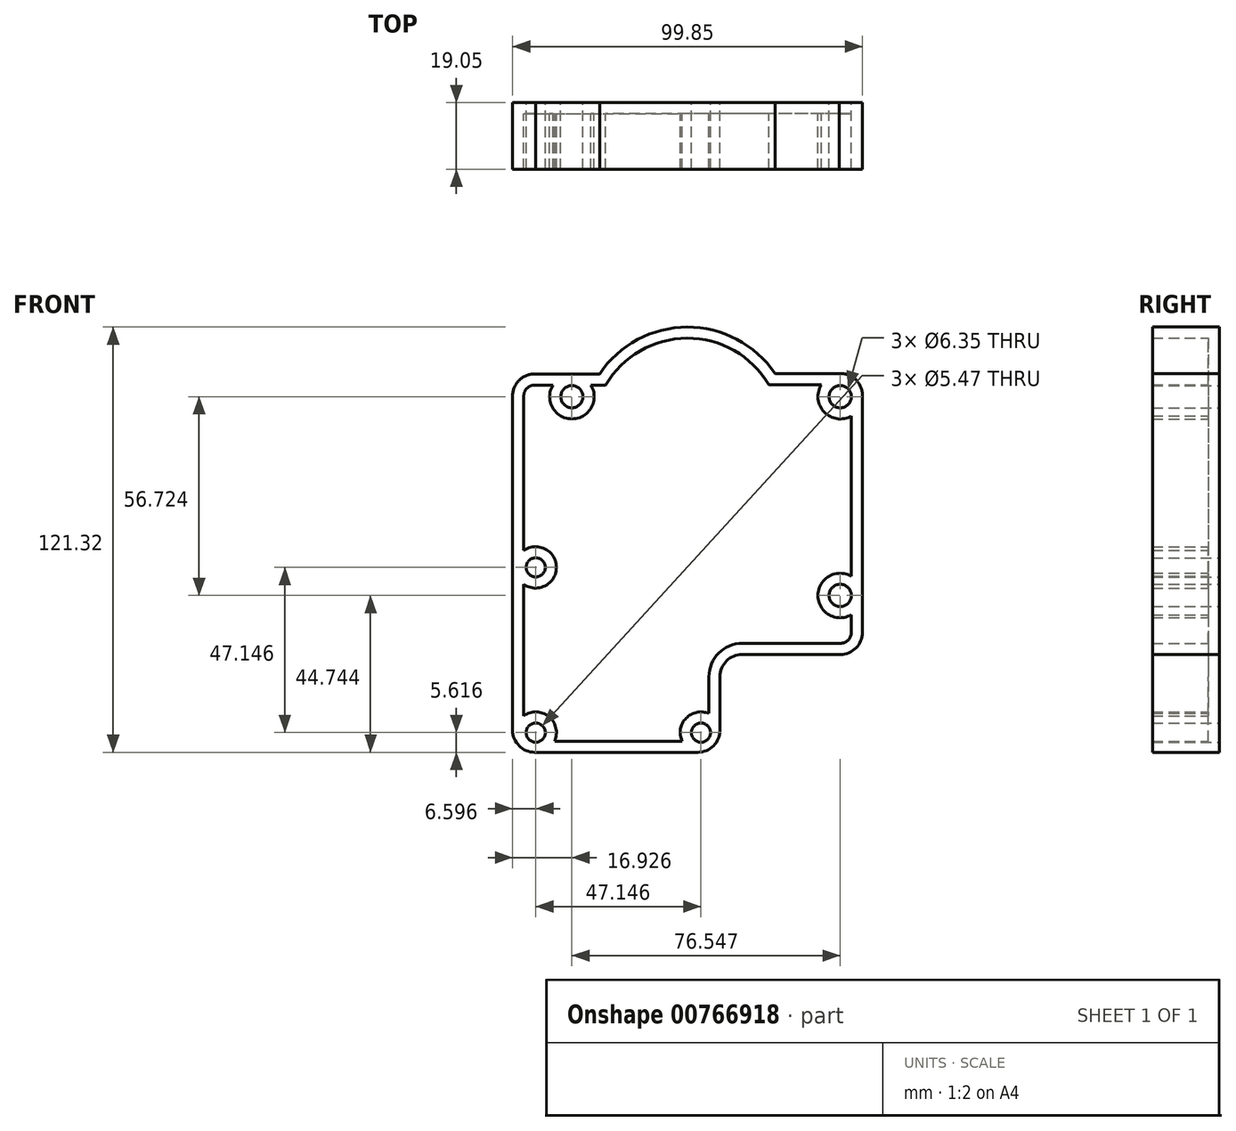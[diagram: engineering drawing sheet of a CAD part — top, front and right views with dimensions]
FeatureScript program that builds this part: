
annotation { "Feature Type Name" : "Feature", "Feature Type Description" : "" }
export const myFeature = defineFeature(function(context is Context, id is Id, definition is map)
    precondition{}
    {
        {
            var Q0;
            Q0=qCreatedBy(makeId("Front.planeOp"),FACE);
            var sketch = newSketch(context, id + "F0", { "sketchPlane" : qUnion([Q0])});
            skLineSegment(sketch, "E0", {"start": v(58.74, 49.1) * mm, "end": v(58.74, -18.36) * mm});
            skLineSegment(sketch, "E1", {"start": v(52.39, -24.71) * mm, "end": v(24.42, -24.71) * mm});
            skPoint(sketch, "E2.center", {"position": v(-41.1, 55.45) * mm});
            skPoint(sketch, "E3.2.0", {"position": v(-122.7, 62.18) * mm});
            skPoint(sketch, "E4.center", {"position": v(-10.94, -23.44) * mm});
            skCircle(sketch, "E5", {"center": v(52.36, -7.89) * mm, "radius": 3.18 * mm});
            skCircle(sketch, "E6", {"center": v(52.36, 48.84) * mm, "radius": 3.18 * mm});
            skCircle(sketch, "E7", {"center": v(-24.18, 48.84) * mm, "radius": 3.18 * mm});
            skPoint(sketch, "E8.visualSharp", {"position": v(58.74, 55.45) * mm});
            skArc(sketch, "E8.filletArc", {"start": v(58.74, 49.1) * mm, "mid": v(56.77, 53.7) * mm, "end": v(52.09, 55.44) * mm});
            skPoint(sketch, "E9.visualSharp", {"position": v(58.74, -24.71) * mm});
            skArc(sketch, "E9.filletArc", {"start": v(52.39, -24.71) * mm, "mid": v(56.88, -22.85) * mm, "end": v(58.74, -18.36) * mm});
            skPoint(sketch, "E10.visualSharp", {"position": v(18.07, -46.78) * mm});
            skPoint(sketch, "E11.visualSharp", {"position": v(-41.1, -46.78) * mm});
            skArc(sketch, "E12.filletArc", {"start": v(-34.54, 55.32) * mm, "mid": v(-39.17, 53.53) * mm, "end": v(-41.1, 48.97) * mm});
            skPoint(sketch, "E13.visualSharp", {"position": v(18.07, -24.71) * mm});
            skArc(sketch, "E13.filletArc", {"start": v(24.42, -24.71) * mm, "mid": v(19.93, -26.57) * mm, "end": v(18.07, -31.06) * mm});
            skLineSegment(sketch, "E14", {"start": v(-41.1, 48.97) * mm, "end": v(-41.1, -46.28) * mm});
            skLineSegment(sketch, "E15", {"start": v(-34.76, -52.63) * mm, "end": v(11.72, -52.63) * mm});
            skLineSegment(sketch, "E16", {"start": v(18.07, -46.28) * mm, "end": v(18.07, -31.06) * mm});
            skPoint(sketch, "E17.visualSharp", {"position": v(18.07, -52.63) * mm});
            skArc(sketch, "E17.filletArc", {"start": v(11.72, -52.63) * mm, "mid": v(16.21, -50.77) * mm, "end": v(18.07, -46.28) * mm});
            skPoint(sketch, "E18.visualSharp", {"position": v(-41.1, -52.63) * mm});
            skArc(sketch, "E18.filletArc", {"start": v(-41.1, -46.28) * mm, "mid": v(-39.25, -50.77) * mm, "end": v(-34.76, -52.63) * mm});
            skLineSegment(sketch, "E19", {"start": v(-34.54, 55.32) * mm, "end": v(-16.29, 55.32) * mm});
            skLineSegment(sketch, "E20", {"start": v(52.09, 55.44) * mm, "end": v(33.73, 55.44) * mm});
            skArc(sketch, "E21", {"start": v(33.73, 55.44) * mm, "mid": v(8.69, 68.7) * mm, "end": v(-16.29, 55.32) * mm});
            skCircle(sketch, "E22", {"center": v(-34.51, 0.13) * mm, "radius": 2.73 * mm});
            skCircle(sketch, "E23.1.0", {"center": v(-34.51, -47.01) * mm, "radius": 2.73 * mm});
            skCircle(sketch, "E23.2.0", {"center": v(12.63, -47.01) * mm, "radius": 2.73 * mm});
            skSolve(sketch);
        }
        {
            var Q0;
            Q0 = qSketchRegion(id + "F0", true);
            extrude(context, id + "F1", {"entities" : qUnion([Q0]), "depth" : 19.05 * mm, "offsetDistance" : 25.4 * mm});
        }
        {
            var Q0;
            Q0=makeQuery(id+"F1.opExtrude","CAP_FACE",FACE,{"disambiguationData":[OSD([sQuery(id+"F0.wireOp",EDGE,"E0"),sQuery(id+"F0.wireOp",EDGE,"E1"),sQuery(id+"F0.wireOp",EDGE,"E5"),sQuery(id+"F0.wireOp",EDGE,"E6"),sQuery(id+"F0.wireOp",EDGE,"E7"),sQuery(id+"F0.wireOp",EDGE,"E8.filletArc"),sQuery(id+"F0.wireOp",EDGE,"E9.filletArc"),sQuery(id+"F0.wireOp",EDGE,"E12.filletArc"),sQuery(id+"F0.wireOp",EDGE,"E13.filletArc"),sQuery(id+"F0.wireOp",EDGE,"E14"),sQuery(id+"F0.wireOp",EDGE,"E15"),sQuery(id+"F0.wireOp",EDGE,"E16"),sQuery(id+"F0.wireOp",EDGE,"E17.filletArc"),sQuery(id+"F0.wireOp",EDGE,"E18.filletArc"),sQuery(id+"F0.wireOp",EDGE,"E19"),sQuery(id+"F0.wireOp",EDGE,"E20"),sQuery(id+"F0.wireOp",EDGE,"E21"),sQuery(id+"F0.wireOp",EDGE,"E22"),sQuery(id+"F0.wireOp",EDGE,"E23.1.0"),sQuery(id+"F0.wireOp",EDGE,"E23.2.0")])],"isStart":false});
            shell(context, id + "F2", {"entities" : qUnion([Q0]), "thickness" : 3.17 * mm});
        }
    });
